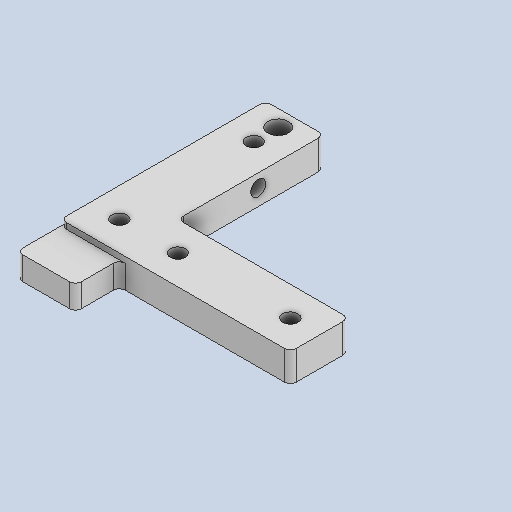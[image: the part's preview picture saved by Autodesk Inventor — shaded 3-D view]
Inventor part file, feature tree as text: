
AUTODESK INVENTOR PART (.ipt)
format: ipt  version: 2024.2 (Build 282272000, 272)  size: 221,696 bytes
history: native  units: in
note: dims shown in document units (in); Inventor stores cm internally (conversion verified against a paired STEP export)
features: fillet x1
ambient origin geometry x8: Origin, YZ Plane, XZ Plane, XY Plane, X Axis, Y Axis, Z Axis, Center Point
bodies: Solid1 (feature_tree)
feature tree (1):
  fillet  "Fillet4"  [1 undecoded]
note: 1 required parameter value undecoded (feature->parameter linkage not recoverable at this tier; creation-order binding heuristic only, values carry confidence <= 0.55)
